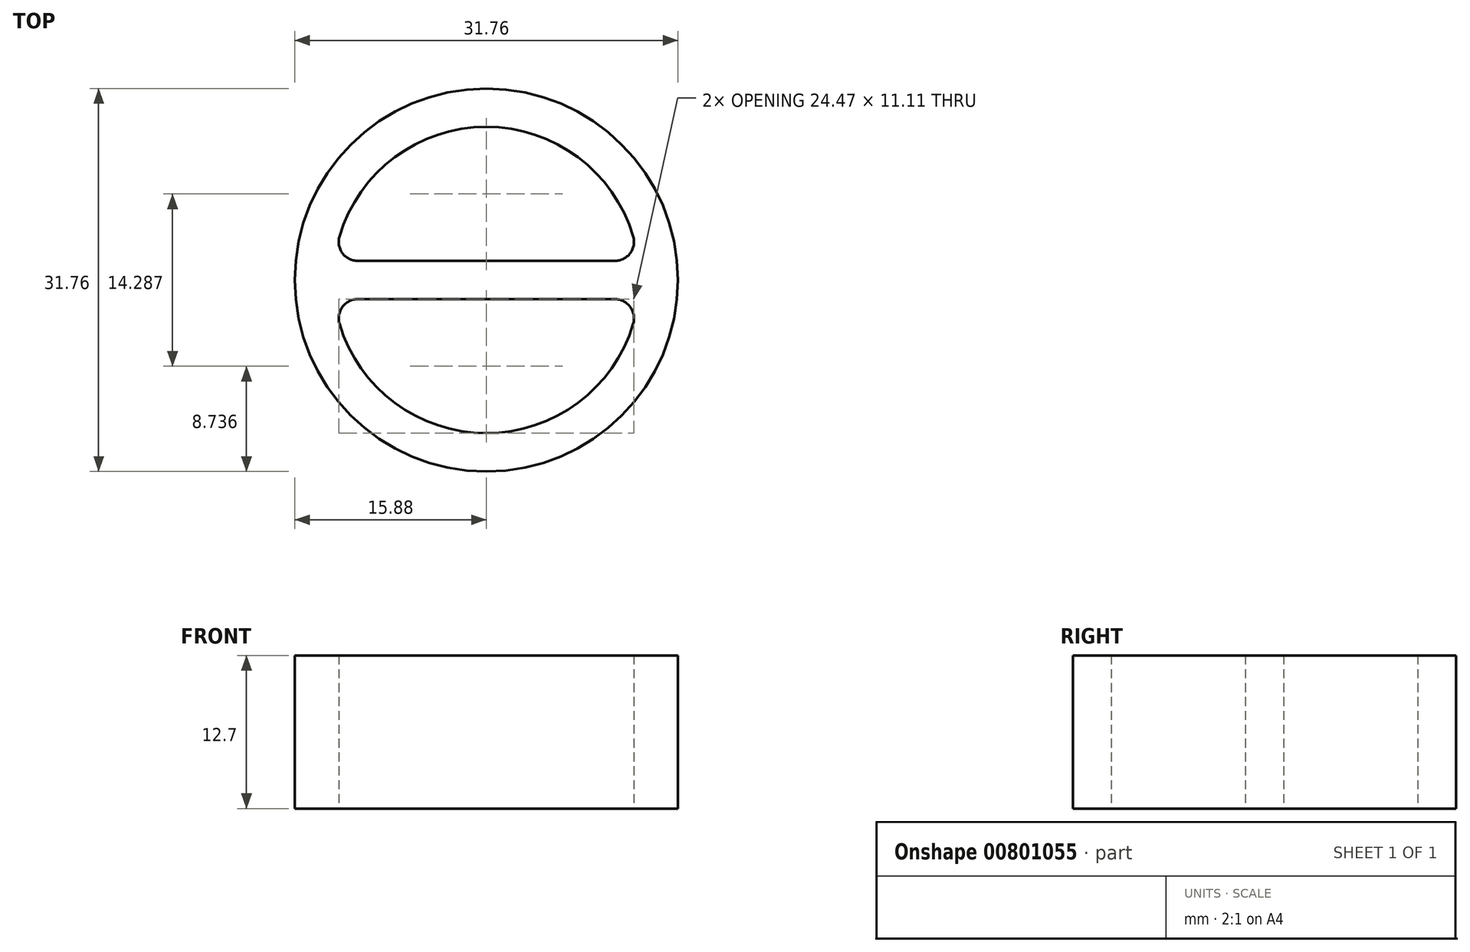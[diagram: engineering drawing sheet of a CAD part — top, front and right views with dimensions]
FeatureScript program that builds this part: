
annotation { "Feature Type Name" : "Feature", "Feature Type Description" : "" }
export const myFeature = defineFeature(function(context is Context, id is Id, definition is map)
    precondition{}
    {
        {
            var Q0;
            Q0=qCreatedBy(makeId("Top.planeOp"),FACE);
            var sketch = newSketch(context, id + "F0", { "sketchPlane" : qUnion([Q0])});
            skArc(sketch, "E0", {"start": v(-12.17, -3.63) * mm, "mid": v(0, -12.7) * mm, "end": v(12.17, -3.63) * mm});
            skCircle(sketch, "E1", {"center": v(0, 0) * mm, "radius": 15.88 * mm});
            skLineSegment(sketch, "E2", {"start": v(-10.65, 1.59) * mm, "end": v(10.65, 1.59) * mm});
            skLineSegment(sketch, "E3", {"start": v(-10.65, -1.59) * mm, "end": v(10.65, -1.59) * mm});
            skArc(sketch, "E4.trimOffspring", {"start": v(12.17, 3.63) * mm, "mid": v(0, 12.7) * mm, "end": v(-12.17, 3.63) * mm});
            skPoint(sketch, "E5.visualSharp", {"position": v(-12.6, 1.59) * mm});
            skArc(sketch, "E5.filletArc", {"start": v(-12.17, 3.63) * mm, "mid": v(-11.92, 2.23) * mm, "end": v(-10.65, 1.59) * mm});
            skPoint(sketch, "E6.visualSharp", {"position": v(12.6, 1.59) * mm});
            skArc(sketch, "E6.filletArc", {"start": v(10.65, 1.59) * mm, "mid": v(11.92, 2.23) * mm, "end": v(12.17, 3.63) * mm});
            skPoint(sketch, "E7.visualSharp", {"position": v(-12.6, -1.59) * mm});
            skArc(sketch, "E7.filletArc", {"start": v(-10.65, -1.59) * mm, "mid": v(-11.92, -2.23) * mm, "end": v(-12.17, -3.63) * mm});
            skPoint(sketch, "E8.visualSharp", {"position": v(12.6, -1.59) * mm});
            skArc(sketch, "E8.filletArc", {"start": v(12.17, -3.63) * mm, "mid": v(11.92, -2.23) * mm, "end": v(10.65, -1.59) * mm});
            skLineSegment(sketch, "E9", {"start": v(-15.88, 0) * mm, "end": v(15.88, 0) * mm});
            skSolve(sketch);
        }
        {
            var Q0;
            Q0 = qSketchRegion(id + "F0", true);
            extrude(context, id + "F1", {"entities" : qUnion([Q0]), "depth" : 12.7 * mm, "offsetDistance" : 25.4 * mm});
        }
        {
            var Q0;
            Q0=qCreatedBy(makeId("Top.planeOp"),FACE);
            cPlane(context, id + "F2", {"entities" : qUnion([Q0]), "cplaneType" : CPlaneType.OFFSET, "offset" : 25.4 * mm, "width" : 152.4 * mm, "height" : 152.4 * mm});
        }
    });
